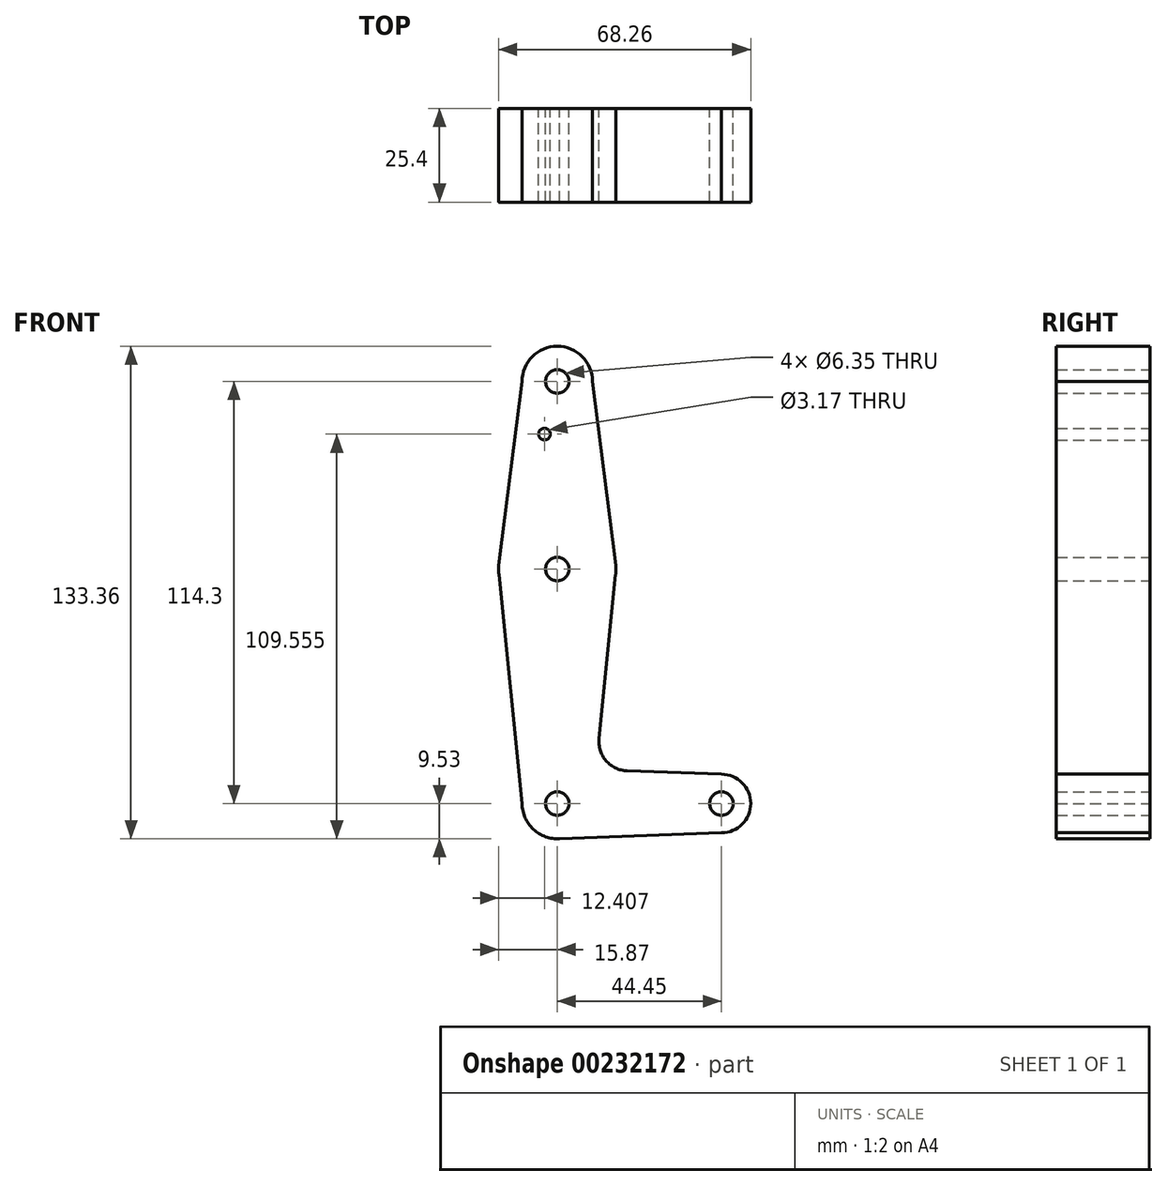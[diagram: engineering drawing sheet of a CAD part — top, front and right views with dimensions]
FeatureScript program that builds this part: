
annotation { "Feature Type Name" : "Feature", "Feature Type Description" : "" }
export const myFeature = defineFeature(function(context is Context, id is Id, definition is map)
    precondition{}
    {
        {
            var Q0;
            Q0=qCreatedBy(makeId("Front.planeOp"),FACE);
            var sketch = newSketch(context, id + "F0", { "sketchPlane" : qUnion([Q0])});
            skCircle(sketch, "E0", {"center": v(0, 0) * mm, "radius": 9.53 * mm});
            skLineSegment(sketch, "E1", {"start": v(0, 0) * mm, "end": v(44.45, 0) * mm});
            skCircle(sketch, "E2", {"center": v(44.45, 0) * mm, "radius": 7.94 * mm});
            skCircle(sketch, "E3", {"center": v(0, 63.5) * mm, "radius": 15.88 * mm});
            skCircle(sketch, "E4", {"center": v(0, 114.3) * mm, "radius": 9.53 * mm});
            skLineSegment(sketch, "E5", {"start": v(-9.53, 0) * mm, "end": v(-15.8, 61.9) * mm});
            skLineSegment(sketch, "E6", {"start": v(15.8, 61.9) * mm, "end": v(11.3, 17.6) * mm});
            skLineSegment(sketch, "E7", {"start": v(9.53, 114.3) * mm, "end": v(15.75, 65.5) * mm});
            skLineSegment(sketch, "E8", {"start": v(-9.53, 114.3) * mm, "end": v(-15.75, 65.5) * mm});
            skLineSegment(sketch, "E9", {"start": v(18.93, 8.85) * mm, "end": v(44.45, 7.94) * mm});
            skArc(sketch, "E10.filletArc", {"start": v(11.3, 17.6) * mm, "mid": v(13.22, 11.57) * mm, "end": v(18.93, 8.85) * mm});
            skCircle(sketch, "E11", {"center": v(0, 63.5) * mm, "radius": 3.18 * mm});
            skCircle(sketch, "E12", {"center": v(0, 114.3) * mm, "radius": 3.18 * mm});
            skCircle(sketch, "E13", {"center": v(0, 0) * mm, "radius": 3.18 * mm});
            skCircle(sketch, "E14", {"center": v(44.45, 0) * mm, "radius": 3.18 * mm});
            skCircle(sketch, "E15", {"center": v(-3.46, 100.03) * mm, "radius": 1.59 * mm});
            skLineSegment(sketch, "E16", {"start": v(0, -9.52) * mm, "end": v(44.45, -7.94) * mm});
            skSolve(sketch);
        }
        {
            var Q0;
            Q0 = qSketchRegion(id + "F0", true);
            extrude(context, id + "F1", {"entities" : qUnion([Q0]), "depth" : 25.4 * mm});
        }
    });
